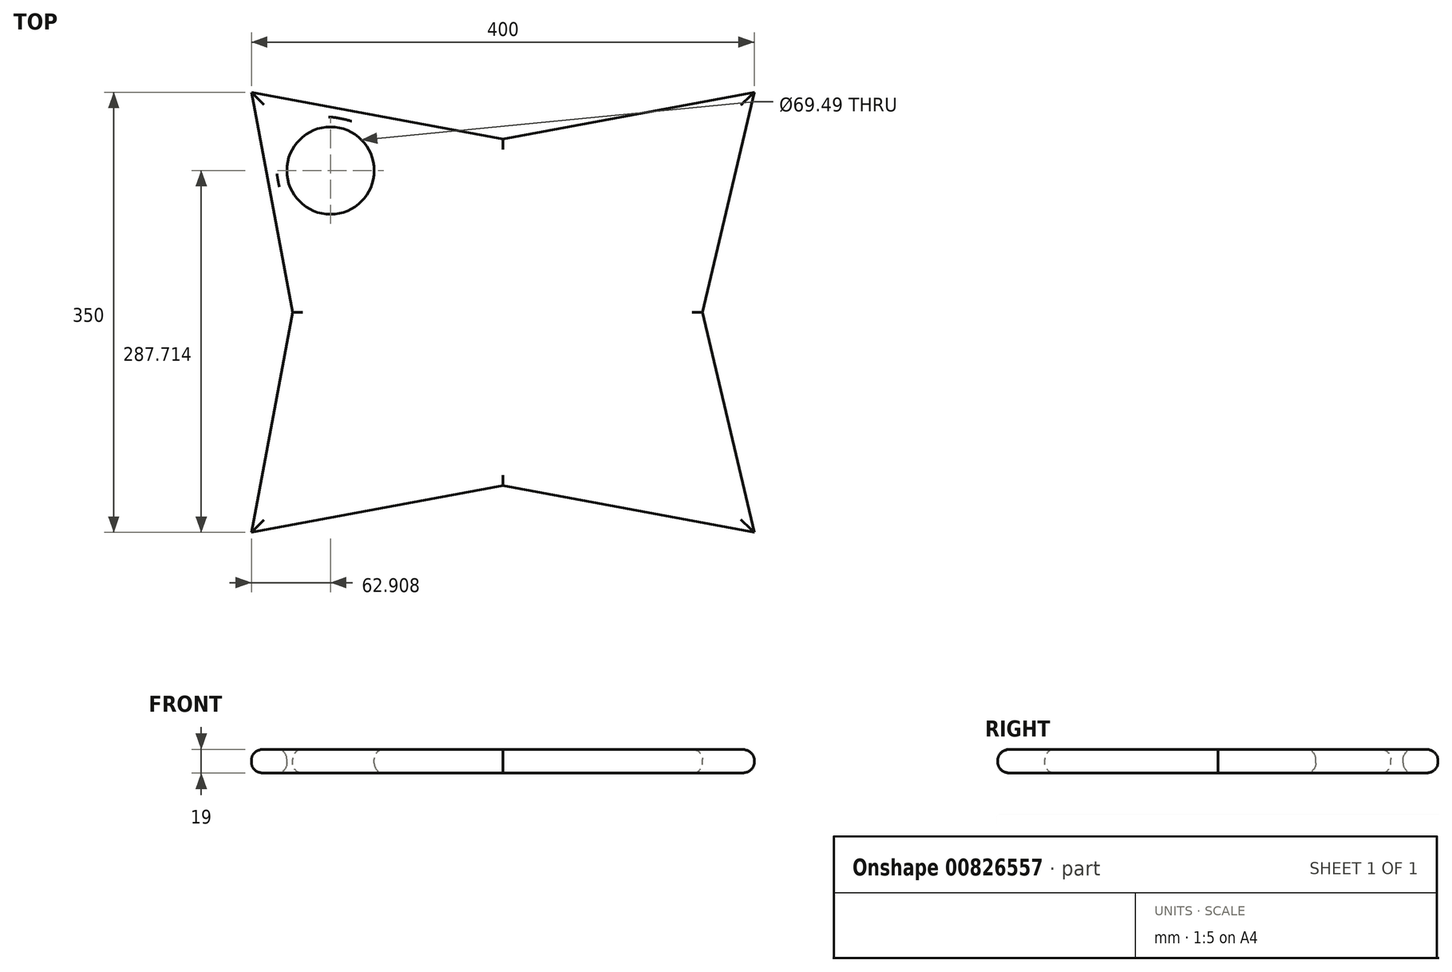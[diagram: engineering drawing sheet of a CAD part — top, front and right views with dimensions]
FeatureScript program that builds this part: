
annotation { "Feature Type Name" : "Feature", "Feature Type Description" : "" }
export const myFeature = defineFeature(function(context is Context, id is Id, definition is map)
    precondition{}
    {
        {
            var Q0;
            Q0=qCreatedBy(makeId("Top.planeOp"),FACE);
            var sketch = newSketch(context, id + "F0", { "sketchPlane" : qUnion([Q0])});
            skLineSegment(sketch, "E0.bottom", {"start": v(-200, 175) * mm, "end": v(200, 175) * mm});
            skLineSegment(sketch, "E0.top", {"start": v(-200, -175) * mm, "end": v(200, -175) * mm});
            skLineSegment(sketch, "E0.left", {"start": v(-200, 175) * mm, "end": v(-200, -175) * mm});
            skLineSegment(sketch, "E0.right", {"start": v(200, 175) * mm, "end": v(200, -175) * mm});
            skPoint(sketch, "E0.middle", {"position": v(0, 0) * mm});
            skSolve(sketch);
        }
        {
            var Q0;
            Q0 = qSketchRegion(id + "F0", true);
            extrude(context, id + "F1", {"entities" : qUnion([Q0]), "depth" : 19 * mm, "offsetDistance" : 25 * mm});
        }
        {
            var Q0;
            Q0=makeQuery(id+"F1.opExtrude","CAP_FACE",FACE,{"disambiguationData":[OSD([sQuery(id+"F0.wireOp",EDGE,"E0.bottom"),sQuery(id+"F0.wireOp",EDGE,"E0.top"),sQuery(id+"F0.wireOp",EDGE,"E0.left"),sQuery(id+"F0.wireOp",EDGE,"E0.right")])],"isStart":false});
            var sketch = newSketch(context, id + "F2", { "sketchPlane" : qUnion([Q0])});
            skLineSegment(sketch, "E1", {"start": v(-200, -175) * mm, "end": v(0, -137.7) * mm});
            skLineSegment(sketch, "E2", {"start": v(200, -175) * mm, "end": v(0, -137.7) * mm});
            skLineSegment(sketch, "E3", {"start": v(200, 175) * mm, "end": v(0, 137.7) * mm});
            skLineSegment(sketch, "E4", {"start": v(0, 137.7) * mm, "end": v(-200, 175) * mm});
            skLineSegment(sketch, "E5", {"start": v(-200, 175) * mm, "end": v(-167.36, 0) * mm});
            skLineSegment(sketch, "E6", {"start": v(-167.36, 0) * mm, "end": v(-200, -175) * mm});
            skLineSegment(sketch, "E7", {"start": v(200, -175) * mm, "end": v(158.8, 0) * mm});
            skLineSegment(sketch, "E8", {"start": v(158.8, 0) * mm, "end": v(200, 175) * mm});
            skSolve(sketch);
        }
        {
            var Q0;
            Q0=makeQuery(id+"F2.imprint","IMPRINT",FACE,{"disambiguationData":[TD([[makeQuery(id+"F2.imprint","IMPRINT",EDGE,{"derivedFrom":sQuery(id+"F2.wireOp",EDGE,"E1")}),-1.0]])]});
            var Q1;
            Q1=makeQuery(id+"F2.imprint","IMPRINT",FACE,{"disambiguationData":[TD([[makeQuery(id+"F2.imprint","IMPRINT",EDGE,{"derivedFrom":sQuery(id+"F2.wireOp",EDGE,"E5")}),-1.0]])]});
            var Q2;
            Q2=makeQuery(id+"F2.imprint","IMPRINT",FACE,{"disambiguationData":[TD([[makeQuery(id+"F2.imprint","IMPRINT",EDGE,{"derivedFrom":sQuery(id+"F2.wireOp",EDGE,"E3")}),-1.0]])]});
            var Q3;
            Q3=makeQuery(id+"F2.imprint","IMPRINT",FACE,{"disambiguationData":[TD([[makeQuery(id+"F2.imprint","IMPRINT",EDGE,{"derivedFrom":sQuery(id+"F2.wireOp",EDGE,"E7")}),-1.0]])]});
            extrude(context, id + "F3", {"entities" : qUnion([Q0, Q1, Q2, Q3]), "operationType" : NewBodyOperationType.REMOVE, "oppositeDirection" : true, "depth" : 25 * mm, "offsetDistance" : 25 * mm});
        }
        {
            var Q0;
            Q0=makeQuery(id+"F1.opExtrude","CAP_FACE",FACE,{"disambiguationData":[OSD([sQuery(id+"F0.wireOp",EDGE,"E0.bottom"),sQuery(id+"F0.wireOp",EDGE,"E0.top"),sQuery(id+"F0.wireOp",EDGE,"E0.left"),sQuery(id+"F0.wireOp",EDGE,"E0.right")])],"isStart":false});
            var sketch = newSketch(context, id + "F4", { "sketchPlane" : qUnion([Q0])});
            skCircle(sketch, "E9", {"center": v(-137.1, 112.71) * mm, "radius": 34.74 * mm});
            skSolve(sketch);
        }
        {
            var Q0;
            Q0=makeQuery(id+"F4.imprint","IMPRINT",FACE,{"disambiguationData":[TD([[makeQuery(id+"F4.imprint","IMPRINT",EDGE,{"derivedFrom":sQuery(id+"F4.wireOp",EDGE,"E9")}),1.0]])]});
            extrude(context, id + "F5", {"entities" : qUnion([Q0]), "operationType" : NewBodyOperationType.REMOVE, "oppositeDirection" : true, "depth" : 25 * mm, "offsetDistance" : 25 * mm});
        }
        {
            var Q0;
            Q0=makeQuery(id+"F1.opExtrude","CAP_FACE",FACE,{"disambiguationData":[OSD([sQuery(id+"F0.wireOp",EDGE,"E0.bottom"),sQuery(id+"F0.wireOp",EDGE,"E0.top"),sQuery(id+"F0.wireOp",EDGE,"E0.left"),sQuery(id+"F0.wireOp",EDGE,"E0.right")])],"isStart":false});
            fillet(context, id + "F6", {"entities" : qUnion([Q0]), "radius" : 8 * mm, "tangentPropagation" : true, "allowEdgeOverflow" : false});
        }
        {
            var Q0;
            Q0=makeQuery(id+"F1.opExtrude","CAP_FACE",FACE,{"disambiguationData":[OSD([sQuery(id+"F0.wireOp",EDGE,"E0.bottom"),sQuery(id+"F0.wireOp",EDGE,"E0.top"),sQuery(id+"F0.wireOp",EDGE,"E0.left"),sQuery(id+"F0.wireOp",EDGE,"E0.right")])],"isStart":true});
            fillet(context, id + "F7", {"entities" : qUnion([Q0]), "radius" : 8 * mm, "tangentPropagation" : true, "allowEdgeOverflow" : false});
        }
    });
